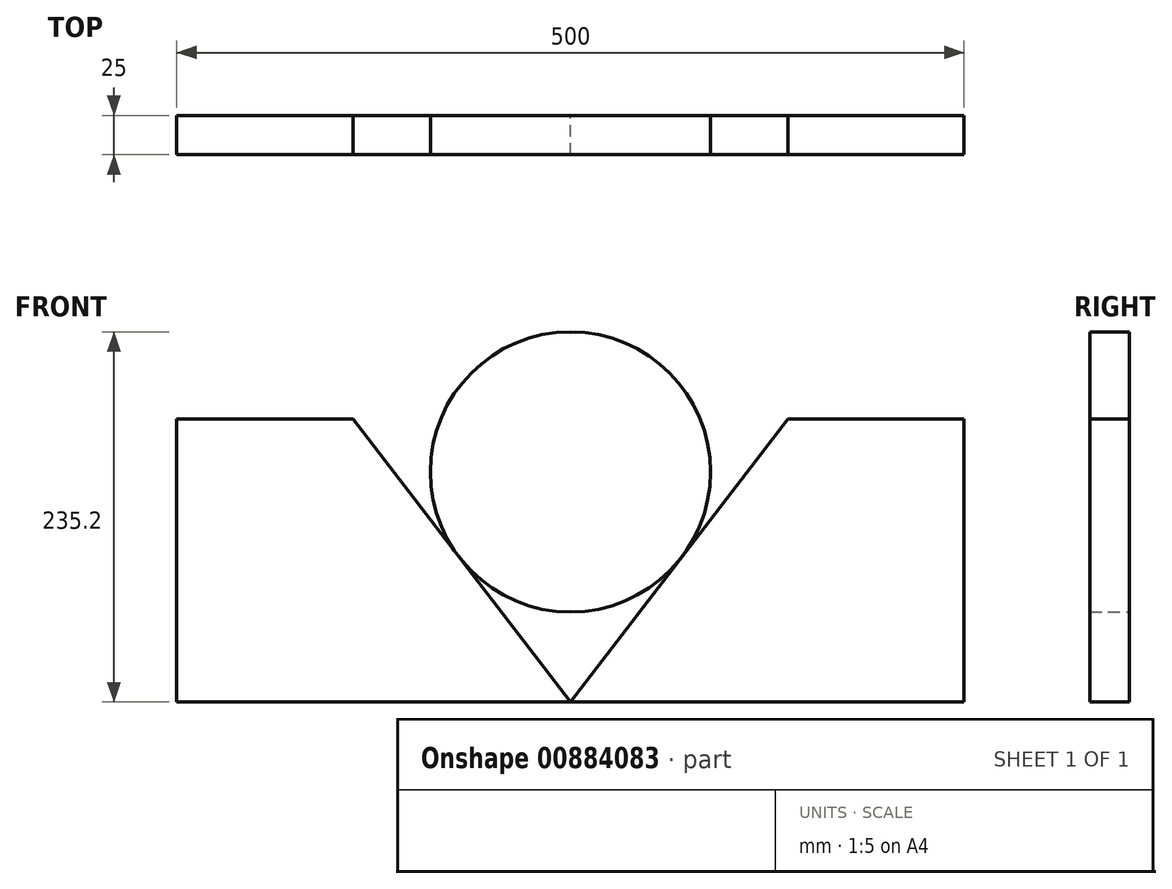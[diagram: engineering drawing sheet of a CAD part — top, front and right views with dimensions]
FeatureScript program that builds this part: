
annotation { "Feature Type Name" : "Feature", "Feature Type Description" : "" }
export const myFeature = defineFeature(function(context is Context, id is Id, definition is map)
    precondition{}
    {
        {
            var Q0;
            Q0=qCreatedBy(makeId("Front.planeOp"),FACE);
            var sketch = newSketch(context, id + "F0", { "sketchPlane" : qUnion([Q0])});
            skLineSegment(sketch, "E0", {"start": v(0, 131.59) * mm, "end": v(0, -143.97) * mm, "construction": true});
            skLineSegment(sketch, "E1", {"start": v(0, 0) * mm, "end": v(250, 0) * mm});
            skLineSegment(sketch, "E2", {"start": v(250, 0) * mm, "end": v(250, 180) * mm});
            skLineSegment(sketch, "E3", {"start": v(250, 180) * mm, "end": v(138.12, 180) * mm});
            skLineSegment(sketch, "E4", {"start": v(138.12, 180) * mm, "end": v(0, 0) * mm});
            skLineSegment(sketch, "E5", {"start": v(250, 0) * mm, "end": v(250, -15) * mm});
            skLineSegment(sketch, "E6", {"start": v(250, -15) * mm, "end": v(250, -53) * mm});
            skLineSegment(sketch, "E7", {"start": v(250, -53) * mm, "end": v(250, -193) * mm});
            skLineSegment(sketch, "E8", {"start": v(250, -193) * mm, "end": v(250, -231) * mm});
            skLineSegment(sketch, "E9", {"start": v(250, -231) * mm, "end": v(0, -231) * mm});
            skLineSegment(sketch, "E10", {"start": v(0, -231) * mm, "end": v(0, 0) * mm});
            skLineSegment(sketch, "E11.MirrorCS", {"start": v(-250, 0) * mm, "end": v(-250, 180) * mm});
            skLineSegment(sketch, "E12.MirrorCS", {"start": v(-138.12, 180) * mm, "end": v(0, 0) * mm});
            skLineSegment(sketch, "E13.MirrorCS", {"start": v(-250, 180) * mm, "end": v(-138.12, 180) * mm});
            skLineSegment(sketch, "E14.MirrorCS", {"start": v(0, 0) * mm, "end": v(-250, 0) * mm});
            skLineSegment(sketch, "E15.MirrorCS", {"start": v(-250, -53) * mm, "end": v(-250, -193) * mm});
            skLineSegment(sketch, "E16.MirrorCS", {"start": v(-250, -15) * mm, "end": v(-250, -53) * mm});
            skLineSegment(sketch, "E17.MirrorCS", {"start": v(-250, 0) * mm, "end": v(-250, -15) * mm});
            skLineSegment(sketch, "E18.MirrorCS", {"start": v(-250, -193) * mm, "end": v(-250, -231) * mm});
            skLineSegment(sketch, "E19.MirrorCS", {"start": v(-250, -231) * mm, "end": v(0, -231) * mm});
            skCircle(sketch, "E20", {"center": v(0, 146.2) * mm, "radius": 89 * mm});
            skPoint(sketch, "E20.first.point", {"position": v(-70.6, 92.02) * mm});
            skPoint(sketch, "E20.second.point", {"position": v(70.6, 92.02) * mm});
            skPoint(sketch, "E20.third.point", {"position": v(65.86, 206.07) * mm});
            skLineSegment(sketch, "E21", {"start": v(250, -15) * mm, "end": v(0, -15) * mm});
            skLineSegment(sketch, "E22", {"start": v(250, -53) * mm, "end": v(0, -53) * mm});
            skLineSegment(sketch, "E23", {"start": v(250, -193) * mm, "end": v(0, -193) * mm});
            skLineSegment(sketch, "E24.MirrorCS", {"start": v(-250, -15) * mm, "end": v(0, -15) * mm});
            skLineSegment(sketch, "E25.MirrorCS", {"start": v(-250, -53) * mm, "end": v(0, -53) * mm});
            skLineSegment(sketch, "E26.MirrorCS", {"start": v(-250, -193) * mm, "end": v(0, -193) * mm});
            skPoint(sketch, "E27", {"position": v(0, 57.2) * mm});
            skSolve(sketch);
        }
        {
            var Q0;
            {var subQ0=sQuery(id+"F0.wireOp",EDGE,"E20");var subQ1=makeQuery(id+"F0.imprint","INTERSECT",VERTEX,{"derivedFrom":[sQuery(id+"F0.wireOp",EDGE,"E4"),subQ0]});Q0=makeQuery(id+"F0.imprint","IMPRINT",FACE,{"disambiguationData":[TD([[makeQuery(id+"F0.imprint","IMPRINT",EDGE,{"disambiguationData":[TD([[subQ1,1.0]])],"derivedFrom":subQ0}),1.0]])]});}
            extrude(context, id + "F1", {"entities" : qUnion([Q0]), "depth" : 25 * mm, "offsetDistance" : 25 * mm});
        }
        {
            var Q0;
            Q0=makeQuery(id+"F0.imprint","IMPRINT",FACE,{"disambiguationData":[TD([[makeQuery(id+"F0.imprint","IMPRINT",EDGE,{"derivedFrom":sQuery(id+"F0.wireOp",EDGE,"E11.MirrorCS")}),-1.0]])]});
            var Q1;
            {var subQ3=sQuery(id+"F0.wireOp",EDGE,"E1");Q1=makeQuery(id+"F0.imprint","IMPRINT",FACE,{"disambiguationData":[TD([[makeQuery(id+"F0.imprint","IMPRINT",EDGE,{"derivedFrom":subQ3}),1.0]])]});}
            extrude(context, id + "F2", {"entities" : qUnion([Q0, Q1]), "operationType" : NewBodyOperationType.ADD, "depth" : 25 * mm, "offsetDistance" : 25 * mm});
        }
    });
